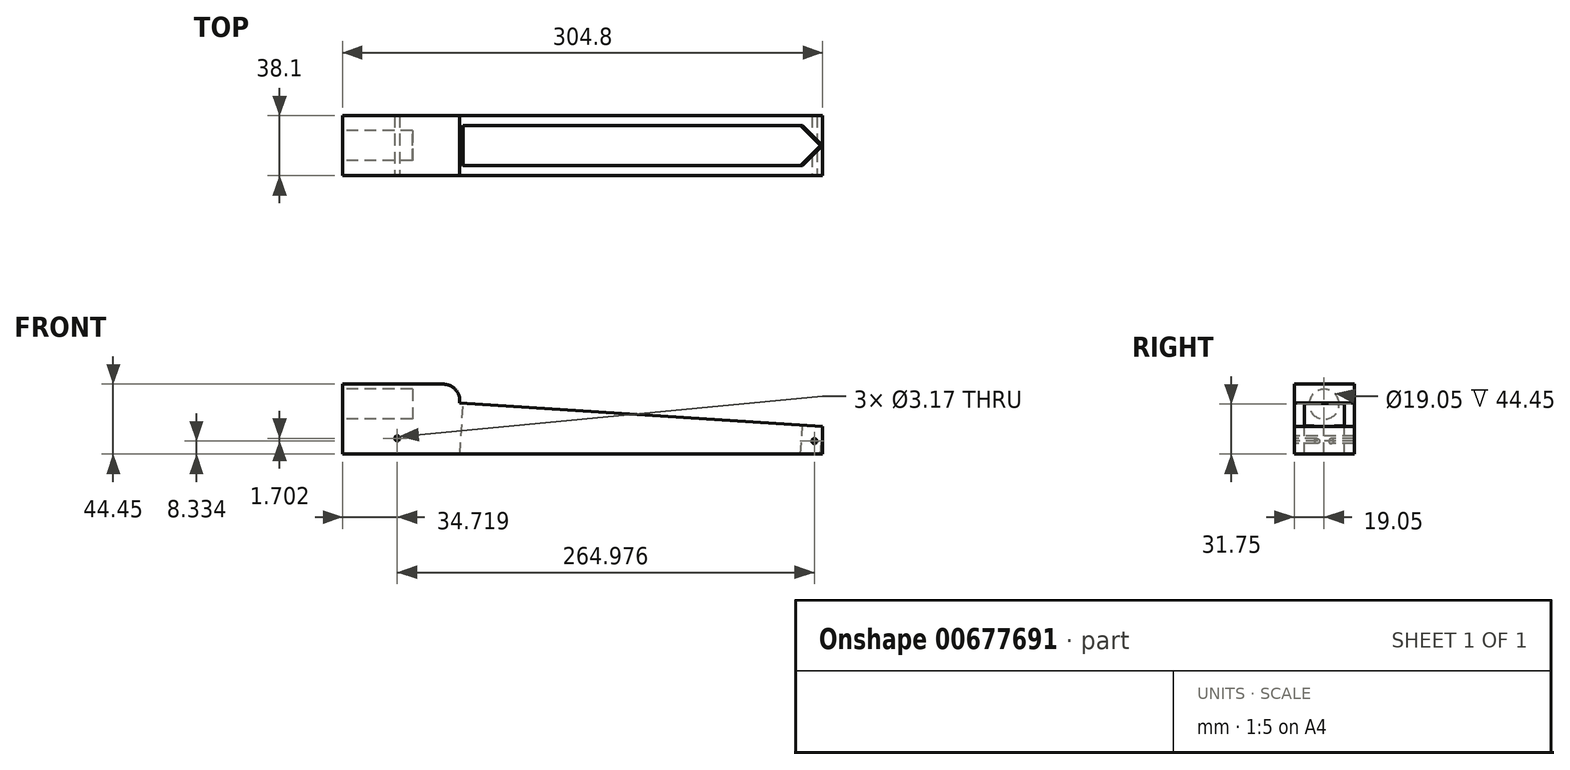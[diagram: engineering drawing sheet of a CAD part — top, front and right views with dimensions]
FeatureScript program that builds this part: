
annotation { "Feature Type Name" : "Feature", "Feature Type Description" : "" }
export const myFeature = defineFeature(function(context is Context, id is Id, definition is map)
    precondition{}
    {
        {
            var Q0;
            Q0=qCreatedBy(makeId("Front.planeOp"),FACE);
            var sketch = newSketch(context, id + "F0", { "sketchPlane" : qUnion([Q0])});
            skLineSegment(sketch, "E0", {"start": v(0, 0) * mm, "end": v(304.8, 0) * mm});
            skLineSegment(sketch, "E1", {"start": v(304.8, 0) * mm, "end": v(304.8, 19.05) * mm});
            skLineSegment(sketch, "E2", {"start": v(0, 0) * mm, "end": v(0, 63.5) * mm});
            skLineSegment(sketch, "E3", {"start": v(0, 63.5) * mm, "end": v(304.8, 19.05) * mm});
            skSolve(sketch);
        }
        {
            var Q0;
            Q0=makeQuery(id+"F0.imprint","IMPRINT",FACE,{"disambiguationData":[TD([[makeQuery(id+"F0.imprint","IMPRINT",EDGE,{"derivedFrom":sQuery(id+"F0.wireOp",EDGE,"E0")}),1.0]])]});
            extrude(context, id + "F1", {"entities" : qUnion([Q0]), "depth" : 38.1 * mm, "offsetDistance" : 25.4 * mm});
        }
        {
            var Q0;
            Q0=makeQuery(id+"F1.opExtrude","SWEPT_FACE",FACE,{"disambiguationData":[OSD([sQuery(id+"F0.wireOp",EDGE,"E2")])]});
            var sketch = newSketch(context, id + "F2", { "sketchPlane" : qUnion([Q0])});
            skCircle(sketch, "E4", {"center": v(19.05, 31.75) * mm, "radius": 9.53 * mm});
            skSolve(sketch);
        }
        {
            var Q0;
            Q0=makeQuery(id+"F2.imprint","IMPRINT",FACE,{"disambiguationData":[TD([[makeQuery(id+"F2.imprint","IMPRINT",EDGE,{"derivedFrom":sQuery(id+"F2.wireOp",EDGE,"E4")}),1.0]])]});
            extrude(context, id + "F3", {"entities" : qUnion([Q0]), "operationType" : NewBodyOperationType.ADD, "oppositeDirection" : true, "depth" : 50.8 * mm, "offsetDistance" : 25.4 * mm});
        }
        {
            var Q0;
            Q0=makeQuery(id+"F1.opExtrude","CAP_FACE",FACE,{"disambiguationData":[OSD([sQuery(id+"F0.wireOp",EDGE,"E0"),sQuery(id+"F0.wireOp",EDGE,"E1"),sQuery(id+"F0.wireOp",EDGE,"E2"),sQuery(id+"F0.wireOp",EDGE,"E3")])],"isStart":false});
            var sketch = newSketch(context, id + "F4", { "sketchPlane" : qUnion([Q0])});
            skSolve(sketch);
        }
        {
            var Q0;
            Q0=makeQuery(id+"F1.opExtrude","SWEPT_FACE",FACE,{"disambiguationData":[OSD([sQuery(id+"F0.wireOp",EDGE,"E2")])]});
            var sketch = newSketch(context, id + "F5", { "sketchPlane" : qUnion([Q0])});
            skCircle(sketch, "E5", {"center": v(19.05, 31.75) * mm, "radius": 9.53 * mm});
            skSolve(sketch);
        }
        {
            var Q0;
            Q0=makeQuery(id+"F5.imprint","IMPRINT",FACE,{"disambiguationData":[TD([[makeQuery(id+"F5.imprint","IMPRINT",EDGE,{"derivedFrom":sQuery(id+"F5.wireOp",EDGE,"E5")}),1.0]])]});
            extrude(context, id + "F6", {"entities" : qUnion([Q0]), "operationType" : NewBodyOperationType.REMOVE, "oppositeDirection" : true, "depth" : 44.45 * mm, "offsetDistance" : 25.4 * mm});
        }
        {
            var Q0;
            Q0=makeQuery(id+"F4.imprint","IMPRINT",FACE,{"disambiguationData":[TD([[makeQuery(id+"F4.imprint","IMPRINT",EDGE,{"derivedFrom":makeQuery(id+"F1.opExtrude","CAP_EDGE",EDGE,{"disambiguationData":[OSD([sQuery(id+"F0.wireOp",EDGE,"E0")])],"isStart":false})}),1.0]])]});
            var sketch = newSketch(context, id + "F7", { "sketchPlane" : qUnion([Q0])});
            skLineSegment(sketch, "E6", {"start": v(0, 44.45) * mm, "end": v(64, 44.45) * mm});
            skArc(sketch, "E7", {"start": v(74.33, 32.44) * mm, "mid": v(71.93, 40.82) * mm, "end": v(64, 44.45) * mm});
            skLineSegment(sketch, "E8", {"start": v(74.33, 32.44) * mm, "end": v(304.8, 17.55) * mm});
            skLineSegment(sketch, "E9", {"start": v(0, 6.35) * mm, "end": v(304.8, 0) * mm});
            skLineSegment(sketch, "E10", {"start": v(304.8, 17.55) * mm, "end": v(304.8, 0) * mm});
            skLineSegment(sketch, "E11", {"start": v(0, 44.45) * mm, "end": v(0, 6.35) * mm});
            skSolve(sketch);
        }
        {
            var Q0;
            {var subQ1=sQuery(id+"F7.wireOp",EDGE,"E6");Q0=makeQuery(id+"F7.imprint","IMPRINT",FACE,{"disambiguationData":[TD([[makeQuery(id+"F7.imprint","IMPRINT",EDGE,{"derivedFrom":subQ1}),1.0]])]});}
            extrude(context, id + "F8", {"entities" : qUnion([Q0]), "operationType" : NewBodyOperationType.REMOVE, "oppositeDirection" : true, "depth" : 46.48 * mm, "offsetDistance" : 25.4 * mm});
        }
        {
            var Q0;
            Q0=makeQuery(id+"F8.boolean.opBoolean","COPY",FACE,{"derivedFrom":makeQuery(id+"F8.opExtrude","SWEPT_FACE",FACE,{"disambiguationData":[OSD([sQuery(id+"F7.wireOp",EDGE,"E8")])]})});
            var sketch = newSketch(context, id + "F9", { "sketchPlane" : qUnion([Q0])});
            skLineSegment(sketch, "E12", {"start": v(290.33, -6.35) * mm, "end": v(74.43, -6.35) * mm});
            skLineSegment(sketch, "E13", {"start": v(290.33, -31.75) * mm, "end": v(74.43, -31.75) * mm});
            skLineSegment(sketch, "E14", {"start": v(74.43, -6.35) * mm, "end": v(74.43, -31.75) * mm});
            skLineSegment(sketch, "E15", {"start": v(303.03, -19.05) * mm, "end": v(290.33, -6.35) * mm});
            skLineSegment(sketch, "E16", {"start": v(303.03, -19.05) * mm, "end": v(290.33, -31.75) * mm});
            skSolve(sketch);
        }
        {
            var Q0;
            Q0=makeQuery(id+"F9.imprint","IMPRINT",FACE,{"disambiguationData":[TD([[makeQuery(id+"F9.imprint","IMPRINT",EDGE,{"derivedFrom":sQuery(id+"F9.wireOp",EDGE,"E12")}),1.0]])]});
            extrude(context, id + "F10", {"entities" : qUnion([Q0]), "operationType" : NewBodyOperationType.REMOVE, "oppositeDirection" : true, "depth" : 38.1 * mm, "offsetDistance" : 25.4 * mm});
        }
        {
            var Q0;
            Q0=makeQuery(id+"F4.imprint","IMPRINT",FACE,{"disambiguationData":[TD([[makeQuery(id+"F4.imprint","IMPRINT",EDGE,{"derivedFrom":makeQuery(id+"F1.opExtrude","CAP_EDGE",EDGE,{"disambiguationData":[OSD([sQuery(id+"F0.wireOp",EDGE,"E0")])],"isStart":false})}),1.0]])]});
            var sketch = newSketch(context, id + "F11", { "sketchPlane" : qUnion([Q0])});
            skCircle(sketch, "E17", {"center": v(34.72, 10.04) * mm, "radius": 1.59 * mm});
            skCircle(sketch, "E18", {"center": v(299.7, 8.33) * mm, "radius": 1.59 * mm});
            skSolve(sketch);
        }
        {
            var Q0;
            Q0 = qSketchRegion(id + "F11", true);
            extrude(context, id + "F12", {"entities" : qUnion([Q0]), "operationType" : NewBodyOperationType.REMOVE, "oppositeDirection" : true, "depth" : 57.15 * mm, "offsetDistance" : 25.4 * mm});
        }
    });
